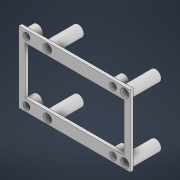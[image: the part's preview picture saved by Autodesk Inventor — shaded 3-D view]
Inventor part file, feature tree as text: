
AUTODESK INVENTOR PART (.ipt)
format: ipt  version: 2021 (Build 250183000, 183)  size: 240,640 bytes
history: native  units: mm
features: extrude x8, sketch x8
ambient origin geometry x8: Origin, YZ Plane, XZ Plane, XY Plane, X Axis, Y Axis, Z Axis, Center Point
bodies: Volumenkörper1 (feature_tree)
feature tree (16):
  extrude  "Extrusion1"  Depth=46.0mm
  extrude  "Extrusion2"  Depth=7.0mm
  extrude  "Extrusion3"  Depth=7.0mm
  extrude  "Extrusion4"  Depth=3.5mm
  extrude  "Extrusion5"  Depth=3.5mm
  extrude  "Extrusion6"  Depth=3.5mm
  extrude  "Extrusion7"  Depth=3.5mm
  extrude  "Extrusion8"  Depth=18.0mm TaperAngle=0.0deg
  sketch  "Skizze1"  dims[d0=57.0mm d1=46.0mm]
  sketch  "Skizze2"  dims[d2=2.0mm d3=0.0mm d4=7.0mm]
  sketch  "Skizze3"  dims[d5=7.0mm d6=7.0mm]
  sketch  "Skizze4"  dims[d7=7.0mm d8=3.5mm]
  sketch  "Skizze5"  dims[d9=3.5mm d10=3.5mm]
  sketch  "Skizze6"  dims[d11=3.5mm d12=3.5mm]
  sketch  "Skizze7"  dims[d13=3.5mm d14=3.5mm]
  sketch  "Skizze8"  dims[d15=3.5mm d16=18.0mm d17=0.0mm d18=5.5mm d19=5.5mm d20=5.5mm d21=5.5mm d22=3.5mm d23=3.5mm d24=3.5mm d25=3.5mm d26=3.5mm d27=3.5mm d28=3.5mm d29=3.5mm d30=4.0mm d31=0.0mm d32=3.2mm d33=3.2mm d34=3.2mm d35=3.2mm d36=4.0mm d37=0.0mm d38=15.0mm d39=0.0mm d40=4.5mm d41=4.5mm d42=4.5mm d43=4.5mm d44=39.0mm d45=39.0mm d46=19.5mm d47=19.5mm d48=19.5mm d49=19.5mm d50=56.0mm d51=5.0mm d53=7.0mm d54=3.5mm d55=5.0mm d56=7.0mm d57=5.0mm d58=3.5mm d59=7.0mm d60=3.5mm d61=11.0mm d62=7.0mm d63=3.5mm d64=11.0mm d65=5.0mm d66=0.0mm d67=6.0mm d68=0.0mm d69=4.0mm d70=7.5mm d71=4.0mm d72=7.5mm d73=6.0mm d74=0.0mm]
